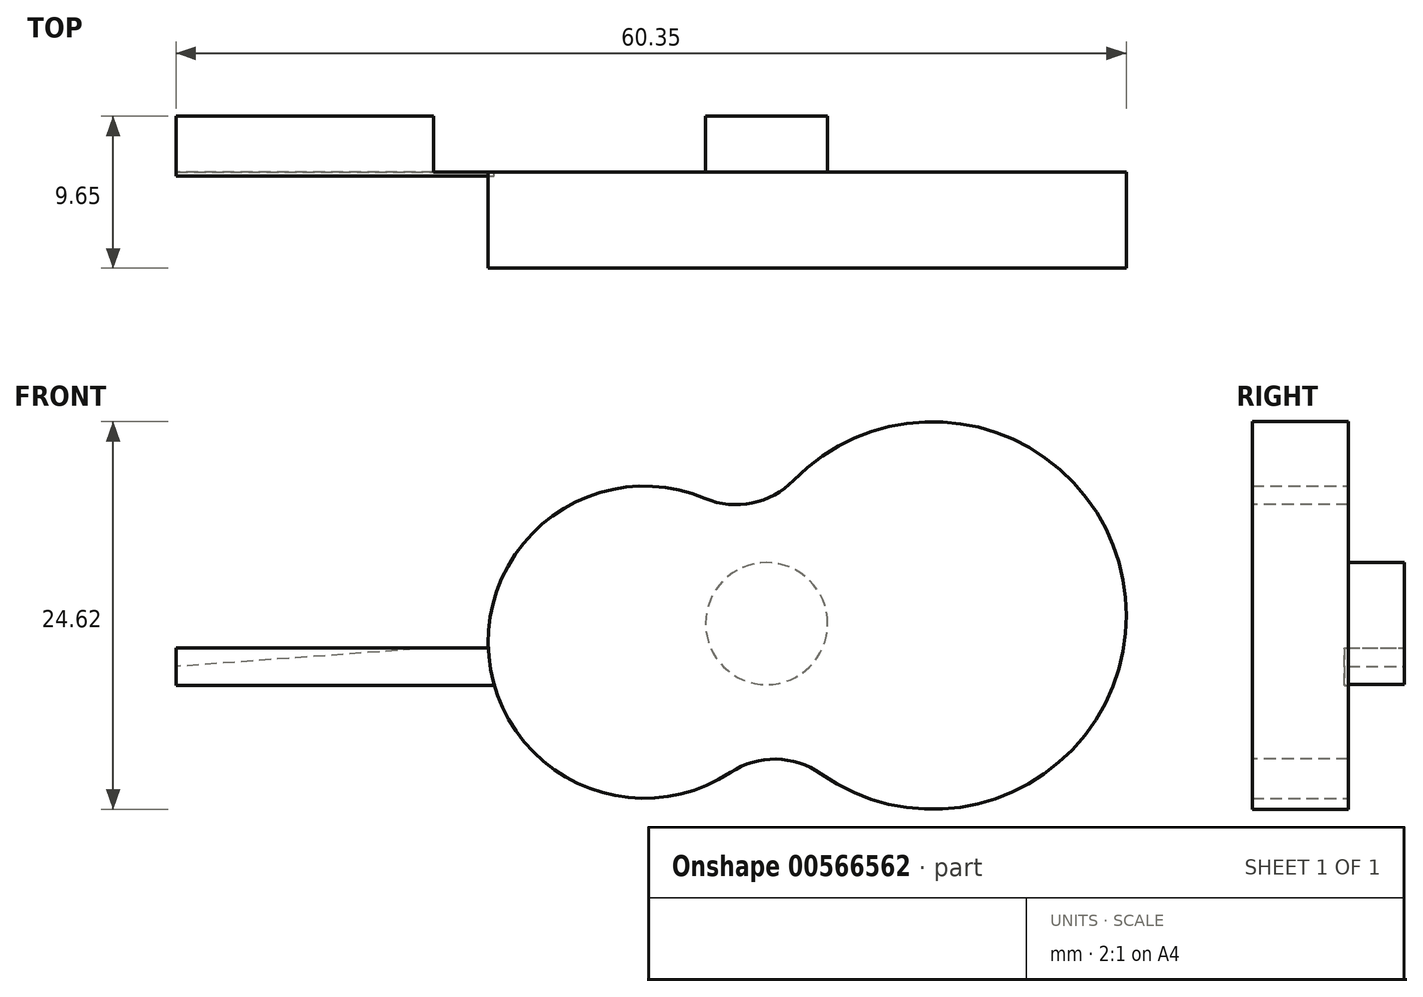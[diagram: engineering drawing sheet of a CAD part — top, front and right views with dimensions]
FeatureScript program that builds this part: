
annotation { "Feature Type Name" : "Feature", "Feature Type Description" : "" }
export const myFeature = defineFeature(function(context is Context, id is Id, definition is map)
    precondition{}
    {
        {
            var Q0;
            Q0=qCreatedBy(makeId("Front.planeOp"),FACE);
            var sketch = newSketch(context, id + "F0", { "sketchPlane" : qUnion([Q0])});
            skArc(sketch, "E0", {"start": v(-32.67, 41.6) * mm, "mid": v(-49.7, 33.8) * mm, "end": v(-31.53, 29.27) * mm});
            skArc(sketch, "E1", {"start": v(-31.53, 29.27) * mm, "mid": v(-9.26, 37.56) * mm, "end": v(-32.67, 41.6) * mm});
            skSolve(sketch);
        }
        {
            var Q0;
            Q0=makeQuery(id+"F0.imprint","IMPRINT",FACE,{"disambiguationData":[TD([[makeQuery(id+"F0.imprint","IMPRINT",EDGE,{"derivedFrom":sQuery(id+"F0.wireOp",EDGE,"E0")}),1.0]])]});
            extrude(context, id + "F1", {"entities" : qUnion([Q0]), "depth" : 9.65 * mm, "offsetDistance" : 25.4 * mm});
        }
        {
            var Q0;
            Q0=qCreatedBy(makeId("Front.planeOp"),FACE);
            var sketch = newSketch(context, id + "F2", { "sketchPlane" : qUnion([Q0])});
            skPoint(sketch, "E2.oppositeSnap0", {"position": v(-49.7, 33.8) * mm});
            skPoint(sketch, "E3", {"position": v(-79.92, 52.27) * mm});
            skPoint(sketch, "E4", {"position": v(-70.94, 47.8) * mm});
            skLineSegment(sketch, "E5", {"start": v(-49.7, 33.8) * mm, "end": v(-69.56, 33.19) * mm});
            skLineSegment(sketch, "E6.bottom", {"start": v(-69.56, 33.19) * mm, "end": v(-46.89, 33.19) * mm});
            skLineSegment(sketch, "E6.top", {"start": v(-69.56, 31.99) * mm, "end": v(-46.89, 31.99) * mm});
            skLineSegment(sketch, "E6.left", {"start": v(-69.56, 33.19) * mm, "end": v(-69.56, 31.99) * mm});
            skLineSegment(sketch, "E6.right", {"start": v(-46.89, 33.19) * mm, "end": v(-46.89, 31.99) * mm});
            skLineSegment(sketch, "E7.top", {"start": v(-69.56, 34.36) * mm, "end": v(-46.89, 34.36) * mm});
            skLineSegment(sketch, "E7.left", {"start": v(-69.56, 33.19) * mm, "end": v(-69.56, 34.36) * mm});
            skLineSegment(sketch, "E7.right", {"start": v(-46.89, 33.19) * mm, "end": v(-46.89, 34.36) * mm});
            skSolve(sketch);
        }
        {
            var Q0;
            Q0=makeQuery(id+"F2.imprint","IMPRINT",FACE,{"disambiguationData":[TD([[makeQuery(id+"F2.imprint","IMPRINT",EDGE,{"derivedFrom":sQuery(id+"F2.wireOp",EDGE,"E6.bottom")}),1.0]])]});
            var Q1;
            Q1=makeQuery(id+"F2.imprint","IMPRINT",FACE,{"disambiguationData":[TD([[makeQuery(id+"F2.imprint","IMPRINT",EDGE,{"derivedFrom":sQuery(id+"F2.wireOp",EDGE,"E6.top")}),1.0]])]});
            extrude(context, id + "F3", {"entities" : qUnion([Q0, Q1]), "operationType" : NewBodyOperationType.ADD, "depth" : 3.8 * mm, "offsetDistance" : 25.4 * mm});
        }
        {
            var Q0;
            {var subQ0=sQuery(id+"F0.wireOp",EDGE,"E1");var subQ1=sQuery(id+"F0.wireOp",EDGE,"E0");Q0=makeQuery(id+"F1.opExtrude","SWEPT_EDGE",EDGE,{"disambiguationData":[OSD([subQ1,subQ0]),TDD([makeQuery(id+"F0.imprint","INTERSECT",VERTEX,{"disambiguationData":[OD(1.0)],"derivedFrom":[subQ1,subQ0]})])]});}
            var Q1;
            {var subQ0=sQuery(id+"F0.wireOp",EDGE,"E1");var subQ1=sQuery(id+"F0.wireOp",EDGE,"E0");Q1=makeQuery(id+"F1.opExtrude","SWEPT_EDGE",EDGE,{"disambiguationData":[OSD([subQ1,subQ0]),TDD([makeQuery(id+"F0.imprint","INTERSECT",VERTEX,{"disambiguationData":[OD(0.0)],"derivedFrom":[subQ1,subQ0]})])]});}
            fillet(context, id + "F4", {"entities" : qUnion([Q0, Q1]), "radius" : 5.08 * mm, "tangentPropagation" : true, "allowEdgeOverflow" : false});
        }
        {
            var Q0;
            Q0=makeQuery(id+"F3.boolean.opBoolean","MERGE",FACE,{"derivedFrom":[makeQuery(id+"F1.opExtrude","CAP_FACE",FACE,{"disambiguationData":[OSD([sQuery(id+"F0.wireOp",EDGE,"E0"),sQuery(id+"F0.wireOp",EDGE,"E1")])],"isStart":true}),makeQuery(id+"F3.opExtrude","CAP_FACE",FACE,{"disambiguationData":[OSD([sQuery(id+"F2.wireOp",EDGE,"E6.top"),sQuery(id+"F2.wireOp",EDGE,"E6.left"),sQuery(id+"F2.wireOp",EDGE,"E6.right"),sQuery(id+"F2.wireOp",EDGE,"E7.top"),sQuery(id+"F2.wireOp",EDGE,"E7.left"),sQuery(id+"F2.wireOp",EDGE,"E7.right")])],"isStart":true})]});
            var sketch = newSketch(context, id + "F5", { "sketchPlane" : qUnion([Q0])});
            skPoint(sketch, "E8.centerSnap0", {"position": v(9.26, 37.56) * mm});
            skLineSegment(sketch, "E9", {"start": v(9.26, 37.56) * mm, "end": v(69.56, 33.18) * mm});
            skCircle(sketch, "E10", {"center": v(32.05, 35.9) * mm, "radius": 3.87 * mm});
            skSolve(sketch);
        }
        {
            var Q0;
            {var subQ0=sQuery(id+"F5.wireOp",EDGE,"E10");var subQ1=sQuery(id+"F5.wireOp",EDGE,"E9");var subQ2=makeQuery(id+"F5.imprint","INTERSECT",VERTEX,{"disambiguationData":[OD(0.0)],"derivedFrom":[subQ1,subQ0]});Q0=makeQuery(id+"F5.imprint","IMPRINT",FACE,{"disambiguationData":[TD([[makeQuery(id+"F5.imprint","IMPRINT",EDGE,{"disambiguationData":[TD([[subQ2,-1.0]])],"derivedFrom":subQ1}),1.0]])]});}
            var Q1;
            {var subQ0=sQuery(id+"F5.wireOp",EDGE,"E10");var subQ1=sQuery(id+"F5.wireOp",EDGE,"E9");var subQ2=makeQuery(id+"F5.imprint","INTERSECT",VERTEX,{"disambiguationData":[OD(0.0)],"derivedFrom":[subQ1,subQ0]});Q1=makeQuery(id+"F5.imprint","IMPRINT",FACE,{"disambiguationData":[TD([[makeQuery(id+"F5.imprint","IMPRINT",EDGE,{"disambiguationData":[TD([[subQ2,-1.0]])],"derivedFrom":subQ1}),-1.0]])]});}
            extrude(context, id + "F6", {"entities" : qUnion([Q0, Q1]), "operationType" : NewBodyOperationType.REMOVE, "oppositeDirection" : true, "depth" : 3.56 * mm, "offsetDistance" : 25.4 * mm});
        }
    });
